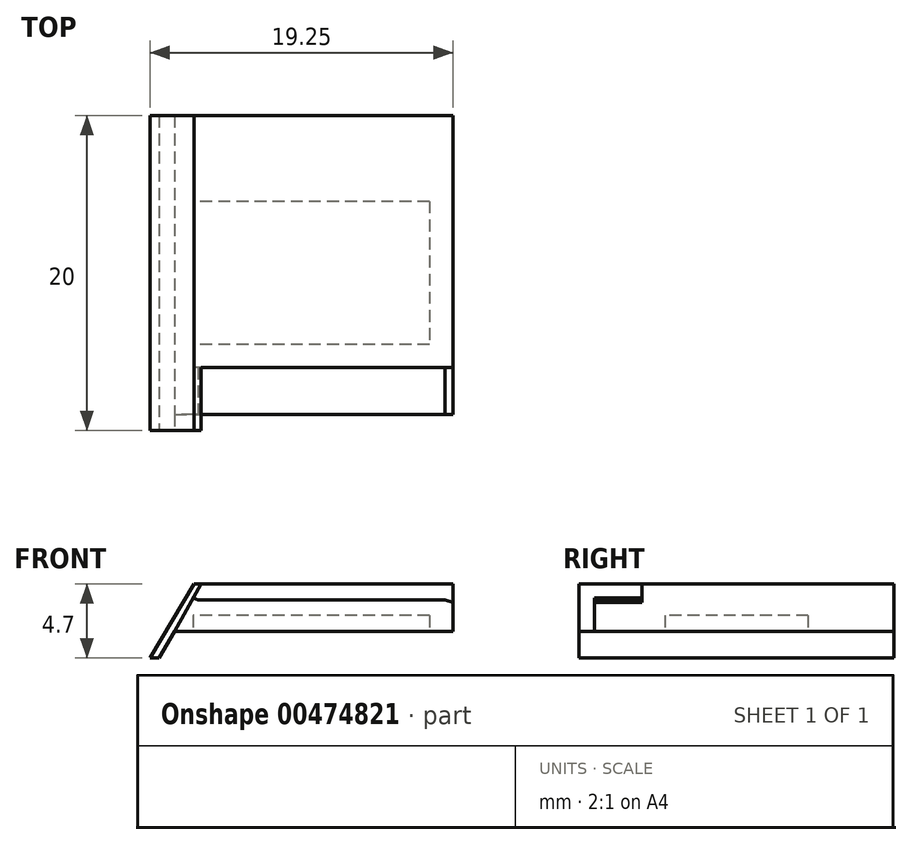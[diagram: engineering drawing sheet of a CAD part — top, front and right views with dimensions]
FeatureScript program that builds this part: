
annotation { "Feature Type Name" : "Feature", "Feature Type Description" : "" }
export const myFeature = defineFeature(function(context is Context, id is Id, definition is map)
    precondition{}
    {
        {
            var Q0;
            Q0=qCreatedBy(makeId("Front.planeOp"),FACE);
            var sketch = newSketch(context, id + "F0", { "sketchPlane" : qUnion([Q0])});
            skLineSegment(sketch, "E0", {"start": v(-19.25, -1.7) * mm, "end": v(-16.45, 3) * mm});
            skLineSegment(sketch, "E1", {"start": v(-16.45, 3) * mm, "end": v(0, 3) * mm});
            skLineSegment(sketch, "E2", {"start": v(0, 3) * mm, "end": v(0, 0) * mm});
            skLineSegment(sketch, "E3", {"start": v(0, 0) * mm, "end": v(-17.08, 0) * mm});
            skLineSegment(sketch, "E4", {"start": v(-17.08, 0) * mm, "end": v(-18.09, -1.7) * mm});
            skLineSegment(sketch, "E5", {"start": v(-18.09, -1.7) * mm, "end": v(-19.25, -1.7) * mm});
            skSolve(sketch);
        }
        {
            var Q0;
            Q0=makeQuery(id+"F0.imprint","IMPRINT",FACE,{"disambiguationData":[TD([[makeQuery(id+"F0.imprint","IMPRINT",EDGE,{"derivedFrom":sQuery(id+"F0.wireOp",EDGE,"E0")}),-1.0]])]});
            extrude(context, id + "F1", {"entities" : qUnion([Q0]), "depth" : 20 * mm});
        }
        {
            var Q0;
            Q0=makeQuery(id+"F1.opExtrude","CAP_FACE",FACE,{"disambiguationData":[OSD([sQuery(id+"F0.wireOp",EDGE,"E0"),sQuery(id+"F0.wireOp",EDGE,"E1"),sQuery(id+"F0.wireOp",EDGE,"E2"),sQuery(id+"F0.wireOp",EDGE,"E3"),sQuery(id+"F0.wireOp",EDGE,"E4"),sQuery(id+"F0.wireOp",EDGE,"E5")])],"isStart":false});
            var sketch = newSketch(context, id + "F2", { "sketchPlane" : qUnion([Q0])});
            skLineSegment(sketch, "E6", {"start": v(-0.5, 2) * mm, "end": v(0, 1.82) * mm});
            skLineSegment(sketch, "E7", {"start": v(0, 1.82) * mm, "end": v(0, 3) * mm});
            skLineSegment(sketch, "E8", {"start": v(0, 3) * mm, "end": v(-16, 3) * mm});
            skLineSegment(sketch, "E9", {"start": v(-0.5, 2) * mm, "end": v(-16.2, 2) * mm});
            skLineSegment(sketch, "E10", {"start": v(-16.2, 2) * mm, "end": v(-16.5, 2.1) * mm});
            skLineSegment(sketch, "E11", {"start": v(-16, 3) * mm, "end": v(-16.5, 2.1) * mm});
            skSolve(sketch);
        }
        {
            var Q0;
            Q0=qSketchRegion(id+"F2",true);
            extrude(context, id + "F3", {"entities" : qUnion([Q0]), "operationType" : NewBodyOperationType.REMOVE, "oppositeDirection" : true, "depth" : 4 * mm});
        }
        {
            var Q0;
            Q0=makeQuery(id+"F1.opExtrude","CAP_FACE",FACE,{"disambiguationData":[OSD([sQuery(id+"F0.wireOp",EDGE,"E0"),sQuery(id+"F0.wireOp",EDGE,"E1"),sQuery(id+"F0.wireOp",EDGE,"E2"),sQuery(id+"F0.wireOp",EDGE,"E3"),sQuery(id+"F0.wireOp",EDGE,"E4"),sQuery(id+"F0.wireOp",EDGE,"E5")])],"isStart":false});
            var sketch = newSketch(context, id + "F4", { "sketchPlane" : qUnion([Q0])});
            skLineSegment(sketch, "E12", {"start": v(0, 1.82) * mm, "end": v(-0.5, 2) * mm});
            skLineSegment(sketch, "E13", {"start": v(-0.5, 2) * mm, "end": v(-16.2, 2) * mm});
            skLineSegment(sketch, "E14", {"start": v(-16.2, 2) * mm, "end": v(-16.5, 2.1) * mm});
            skLineSegment(sketch, "E15", {"start": v(-16.5, 2.1) * mm, "end": v(-17.68, 0) * mm});
            skLineSegment(sketch, "E16", {"start": v(-17.68, 0) * mm, "end": v(0, 0) * mm});
            skLineSegment(sketch, "E17", {"start": v(0, 0) * mm, "end": v(0, 1.82) * mm});
            skSolve(sketch);
        }
        {
            var Q0;
            Q0=qSketchRegion(id+"F4",true);
            extrude(context, id + "F5", {"entities" : qUnion([Q0]), "operationType" : NewBodyOperationType.REMOVE, "oppositeDirection" : true, "depth" : 1 * mm});
        }
        {
            var Q0;
            Q0=makeQuery(id+"F1.opExtrude","CAP_FACE",FACE,{"disambiguationData":[OSD([sQuery(id+"F0.wireOp",EDGE,"E0"),sQuery(id+"F0.wireOp",EDGE,"E1"),sQuery(id+"F0.wireOp",EDGE,"E2"),sQuery(id+"F0.wireOp",EDGE,"E3"),sQuery(id+"F0.wireOp",EDGE,"E4"),sQuery(id+"F0.wireOp",EDGE,"E5")])],"isStart":false});
            var sketch = newSketch(context, id + "F6", { "sketchPlane" : qUnion([Q0])});
            skLineSegment(sketch, "E18", {"start": v(-18.09, -1.7) * mm, "end": v(-17.08, 0) * mm});
            skLineSegment(sketch, "E19", {"start": v(-17.08, 0) * mm, "end": v(-17.68, 0) * mm});
            skLineSegment(sketch, "E20", {"start": v(-17.68, 0) * mm, "end": v(-18.67, -1.7) * mm});
            skLineSegment(sketch, "E21", {"start": v(-18.67, -1.7) * mm, "end": v(-18.09, -1.7) * mm});
            skSolve(sketch);
        }
        {
            var Q0;
            Q0=qSketchRegion(id+"F6",true);
            extrude(context, id + "F7", {"entities" : qUnion([Q0]), "operationType" : NewBodyOperationType.REMOVE, "endBound" : BoundingType.THROUGH_ALL, "oppositeDirection" : true, "depth" : 25 * mm});
        }
        {
            var Q0;
            Q0=makeQuery(id+"F1.opExtrude","SWEPT_FACE",FACE,{"disambiguationData":[OSD([sQuery(id+"F0.wireOp",EDGE,"E1")])]});
            var sketch = newSketch(context, id + "F8", { "sketchPlane" : qUnion([Q0])});
            skLineSegment(sketch, "E22", {"start": v(-16.45, -20) * mm, "end": v(-16.45, 0) * mm, "construction": true});
            skPoint(sketch, "E23", {"position": v(-16.45, -10) * mm});
            skLineSegment(sketch, "E24", {"start": v(-16.45, -10) * mm, "end": v(0, -10) * mm, "construction": true});
            skSolve(sketch);
        }
        {
            var Q0;
            Q0=sQuery(id+"F8.wireOp",EDGE,"E24");
            cPlane(context, id + "F9", {"entities" : qUnion([Q0]), "cplaneType" : CPlaneType.LINE_ANGLE, "offset" : 25 * mm, "angle" : 0 * degree, "width" : 150 * mm, "height" : 150 * mm});
        }
        {
            var Q0;
            Q0=makeQuery(id+"F7.boolean.opBoolean","MERGE",FACE,{"derivedFrom":[makeQuery(id+"F1.opExtrude","SWEPT_FACE",FACE,{"disambiguationData":[OSD([sQuery(id+"F0.wireOp",EDGE,"E3")])]}),makeQuery(id+"F7.opExtrude","SWEPT_FACE",FACE,{"disambiguationData":[OSD([sQuery(id+"F6.wireOp",EDGE,"E19")])]})]});
            var sketch = newSketch(context, id + "F10", { "sketchPlane" : qUnion([Q0])});
            skLineSegment(sketch, "E25.bottom", {"start": v(-1.5, 5.45) * mm, "end": v(-16.5, 5.45) * mm});
            skLineSegment(sketch, "E25.top", {"start": v(-1.5, 14.55) * mm, "end": v(-16.5, 14.55) * mm});
            skLineSegment(sketch, "E25.left", {"start": v(-1.5, 5.45) * mm, "end": v(-1.5, 14.55) * mm});
            skLineSegment(sketch, "E25.right", {"start": v(-16.5, 5.45) * mm, "end": v(-16.5, 14.55) * mm});
            skSolve(sketch);
        }
        {
            var Q0;
            Q0=qSketchRegion(id+"F10",true);
            extrude(context, id + "F11", {"entities" : qUnion([Q0]), "operationType" : NewBodyOperationType.REMOVE, "oppositeDirection" : true, "depth" : 1 * mm});
        }
    });
